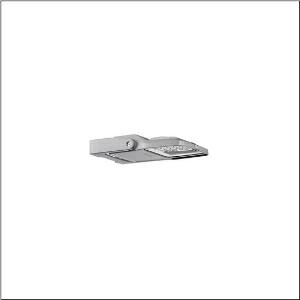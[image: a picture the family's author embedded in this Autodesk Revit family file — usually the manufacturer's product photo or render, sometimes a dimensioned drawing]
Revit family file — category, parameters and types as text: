
# Revit family: floodlight_fl_21_iq_micro___pl52_5xa7762a2d2a_5d06
name_source: partatom
category: Lighting Fixtures
units: mm (PartAtom-declared; Revit-internal decimal feet)

## family parameters
Cut with Voids When Loaded = No
Host = Face
Light Source = No
Part Type = Normal
Room Calculation Point = No
Round Connector Dimension = Use Diameter
Shared = No

## types (1)
- --- (1 x LED, 2890 lm, 23.1 W, 3000K)
    Apparent Load = 23 VA
    CIE Flux Codes = 26 60 98 100 100
    Color Rendering = 70
    Color Temperature = 3000K
    Default Elevation = 1800 mm
    Description = Floodlight FL 21 iQ micro, floodlight, primary light control with lens, of PMMA, primary optical cover: protective disc, of toughened safety glass, transparent, light distribution: PL52, light emission: direct distribution, installation type: surface-mounted, lamps: LED, High Power LED, rated values: 2.890lm | 23,1W | 125,1lm/W (begin service life); end service life: 2.890lm | 23,8W; at 50% lumin. flux: 1.445lm | 11W | 131,4lm/W, colour temperature: 3000K, colour rendering: CRI > 70, light colour: 730, light setting 1 begin service life: 100% | 2.890lm | 23,1W | 125,1lm/W | 3.000K, light setting 1 end service life: 23,8W, further light settings possible, control: Auto-Match, Temp-Guard, Night-Set, Smart-Wire, Desk-Remote (wireless, voltage-free reading and setting of iQ features in the workshop via application-optimized NFC function/RFID function), optimised constant luminous flux control (CLO 2.0), Street-Remote, pre-setting: linear dimming characteristic, with terminal, 6-pole, mains connection: 220..240V, AC, 50/60Hz, luminaire housing, of diecast aluminium, powder-coated, SITECO metallic grey (DB 702S), corrosivity category C5 mid according to DIN EN ISO 12944suitable for swimming poolschlorine-resistant, sealing non-destructively replaceable, design bracket, of diecast aluminium, powder-coated, SITECO metallic grey (DB 702S), protection rating (complete): IP66, insulation class (complete): insulation class II (safety insulation), certification: CE, ENEC, VDE, protection symbol: D, impact resistance: IK07, permissible operating ambient temperature: -40..+40°C, permissible operating ambient temperature for outdoor applications: -40..+50°C, standard: DIN EN 12944, LABS conformity tested according to VDMA 24364:2018-05, packaging unit: 1 piece

Light Distribution: PL52
    Height = 65 mm
    Lamp = 1 x LED
    Lamp Light Flux = 2890 lm
    Lamp Power = 23.1 W
    Lamp count = 1
    Length = 312 mm
    Luminous efficacy = 125 lm/W
    Manufacturer = Siteco
    ModVariant = No
    Model = 5XA7762A2D2A
    Mounting Place = Wall
    Mounting Type = Surface mounted
    Number of Poles = 1
    OnlyDefault = Yes
    Power Factor = 1
    Product Name = Floodlight FL 21 iQ micro | PL52
    Product group = floodlight | wall mounted
    ProductGroupID = 2002
    Protection Class = Protection class II
    Protection Degree = IP 66
    RLX_Detail_Level = 1
    RLX_Emergency_Light_Flux = 0 lm
    RLX_Emergency_Type = 0
    RLX_Emergency_Type_DB = No
    RlxData = <blob elided: 97801 chars, md5=ae2f0bce>
    Socket = socket
    Standby Power = 0 W
    System Light Flux = 2890 lm
    System Power = 23 W
    Type Comments = factory setting: luminous flux: 100 % | dim-lin: 254 | 455 mA
    Type Image = l_1006878.jpg
    URL = http://relux.com
    VarID = @adj_178919
    Voltage = 0 V
    Weight = 0.00 kg
    Width = 230 mm

## geometry (parser evidence)
native form markers: Blend x4, Sweep x12
no freeform markers — native parametric forms only
